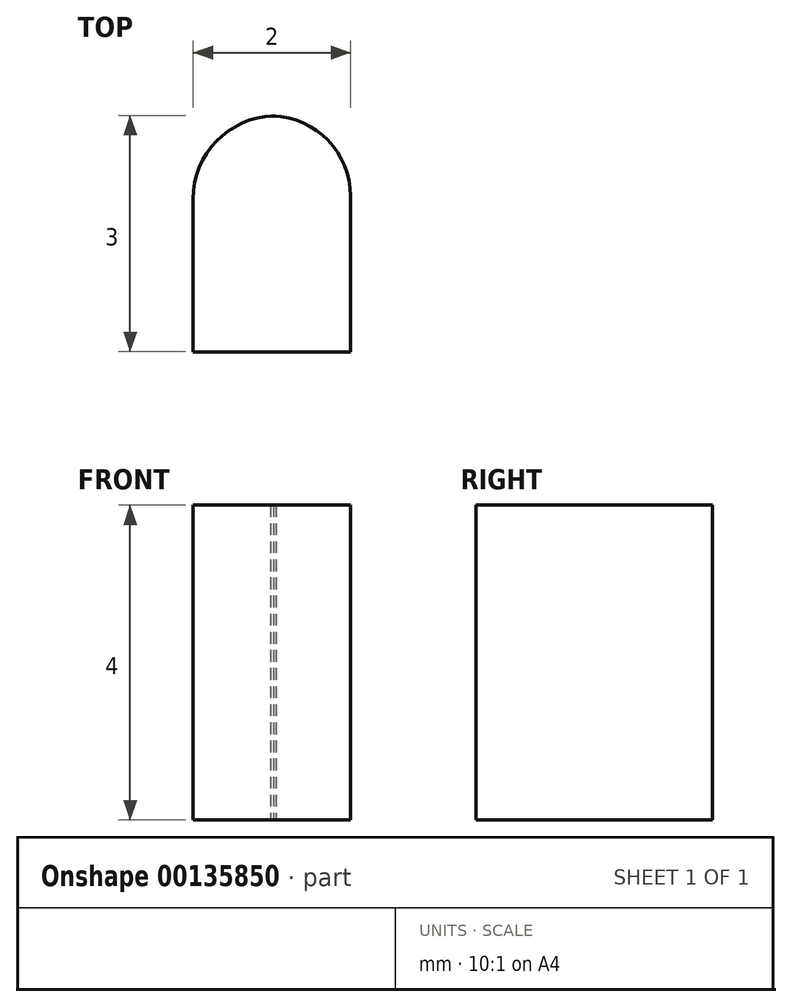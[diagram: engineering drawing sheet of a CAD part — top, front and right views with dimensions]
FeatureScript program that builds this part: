
annotation { "Feature Type Name" : "Feature", "Feature Type Description" : "" }
export const myFeature = defineFeature(function(context is Context, id is Id, definition is map)
    precondition{}
    {
        {
            var Q0;
            Q0=qCreatedBy(makeId("Top.planeOp"),FACE);
            var sketch = newSketch(context, id + "F0", { "sketchPlane" : qUnion([Q0])});
            skLineSegment(sketch, "E0.bottom", {"start": v(-4.58, -6.97) * mm, "end": v(-2.58, -6.97) * mm});
            skLineSegment(sketch, "E0.top", {"start": v(-3.6, -3.97) * mm, "end": v(-3.53, -3.97) * mm});
            skLineSegment(sketch, "E0.left", {"start": v(-4.58, -6.97) * mm, "end": v(-4.58, -5.03) * mm});
            skLineSegment(sketch, "E0.right", {"start": v(-2.58, -6.97) * mm, "end": v(-2.58, -5) * mm});
            skPoint(sketch, "E1.visualSharp", {"position": v(-4.58, -3.97) * mm});
            skArc(sketch, "E1.filletArc", {"start": v(-3.53, -3.97) * mm, "mid": v(-4.27, -4.28) * mm, "end": v(-4.58, -5.03) * mm});
            skPoint(sketch, "E2.visualSharp", {"position": v(-2.58, -3.97) * mm});
            skArc(sketch, "E2.filletArc", {"start": v(-2.58, -5) * mm, "mid": v(-2.88, -4.27) * mm, "end": v(-3.6, -3.97) * mm});
            skSolve(sketch);
        }
        {
            var Q0;
            Q0 = qSketchRegion(id + "F0", true);
            extrude(context, id + "F1", {"entities" : qUnion([Q0]), "depth" : 4 * mm});
        }
    });
